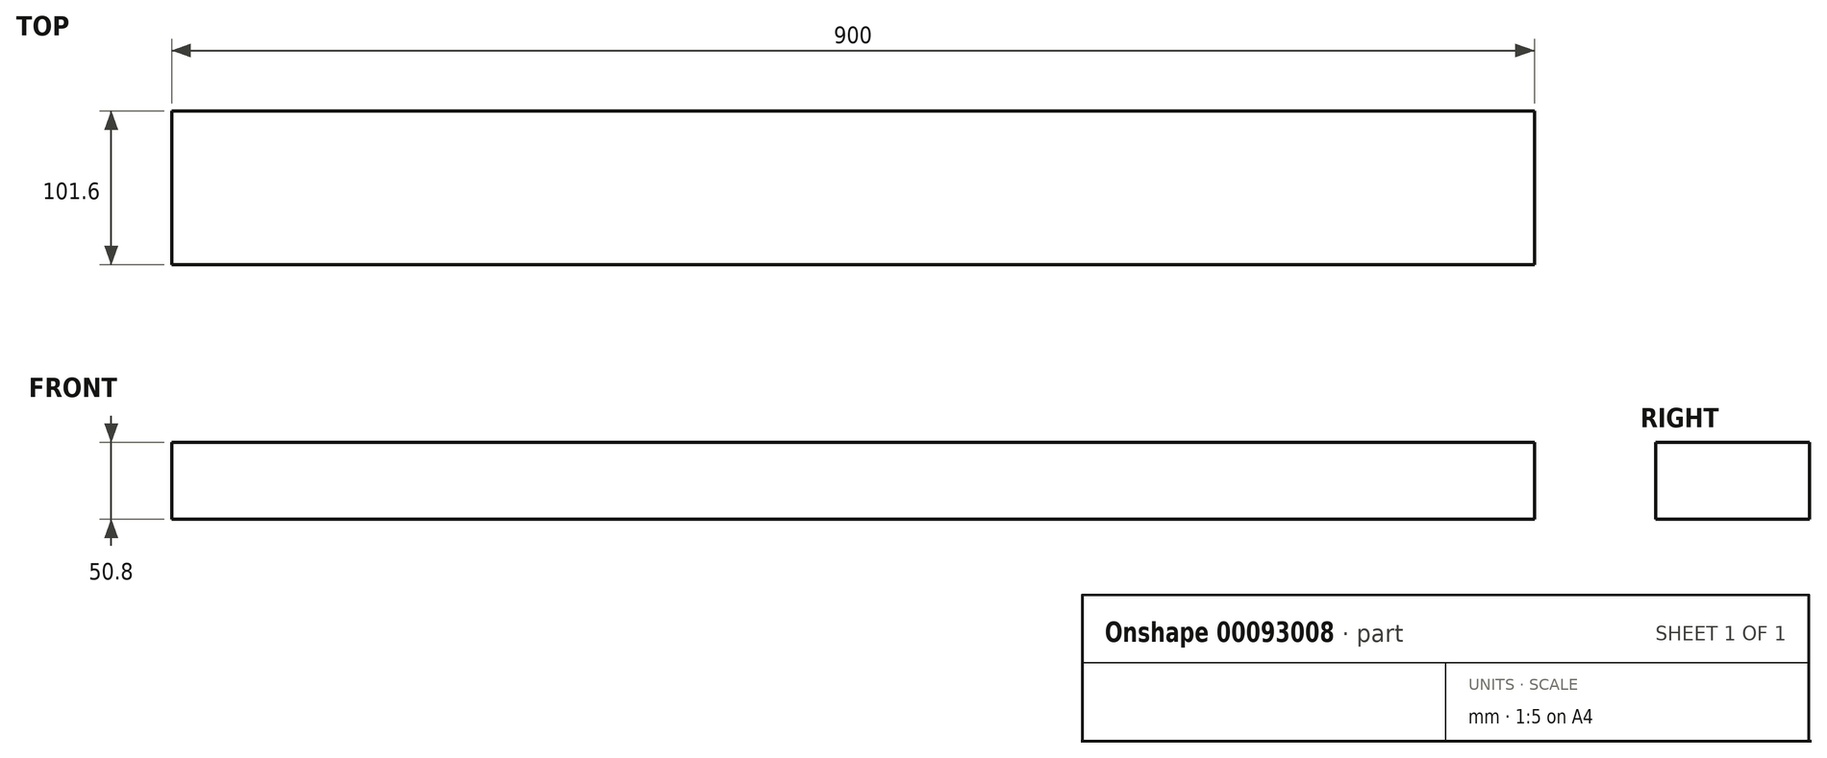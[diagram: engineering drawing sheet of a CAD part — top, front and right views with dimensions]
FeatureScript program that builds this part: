
annotation { "Feature Type Name" : "Feature", "Feature Type Description" : "" }
export const myFeature = defineFeature(function(context is Context, id is Id, definition is map)
    precondition{}
    {
        {
            var Q0;
            Q0=qCreatedBy(makeId("Right.planeOp"),FACE);
            var sketch = newSketch(context, id + "F0", { "sketchPlane" : qUnion([Q0])});
            skLineSegment(sketch, "E0.bottom", {"start": v(-50.8, 50.8) * mm, "end": v(50.8, 50.8) * mm});
            skLineSegment(sketch, "E0.top", {"start": v(-50.8, 0) * mm, "end": v(50.8, 0) * mm});
            skLineSegment(sketch, "E0.left", {"start": v(-50.8, 50.8) * mm, "end": v(-50.8, 0) * mm});
            skLineSegment(sketch, "E0.right", {"start": v(50.8, 50.8) * mm, "end": v(50.8, 0) * mm});
            skSolve(sketch);
        }
        {
            var Q0;
            Q0=makeQuery(id+"F0.imprint","IMPRINT",FACE,{"disambiguationData":[TD([[makeQuery(id+"F0.imprint","IMPRINT",EDGE,{"derivedFrom":sQuery(id+"F0.wireOp",EDGE,"E0.bottom")}),-1.0]])]});
            extrude(context, id + "F1", {"entities" : qUnion([Q0]), "endBound" : BoundingType.SYMMETRIC, "depth" : 900 * mm});
        }
    });
